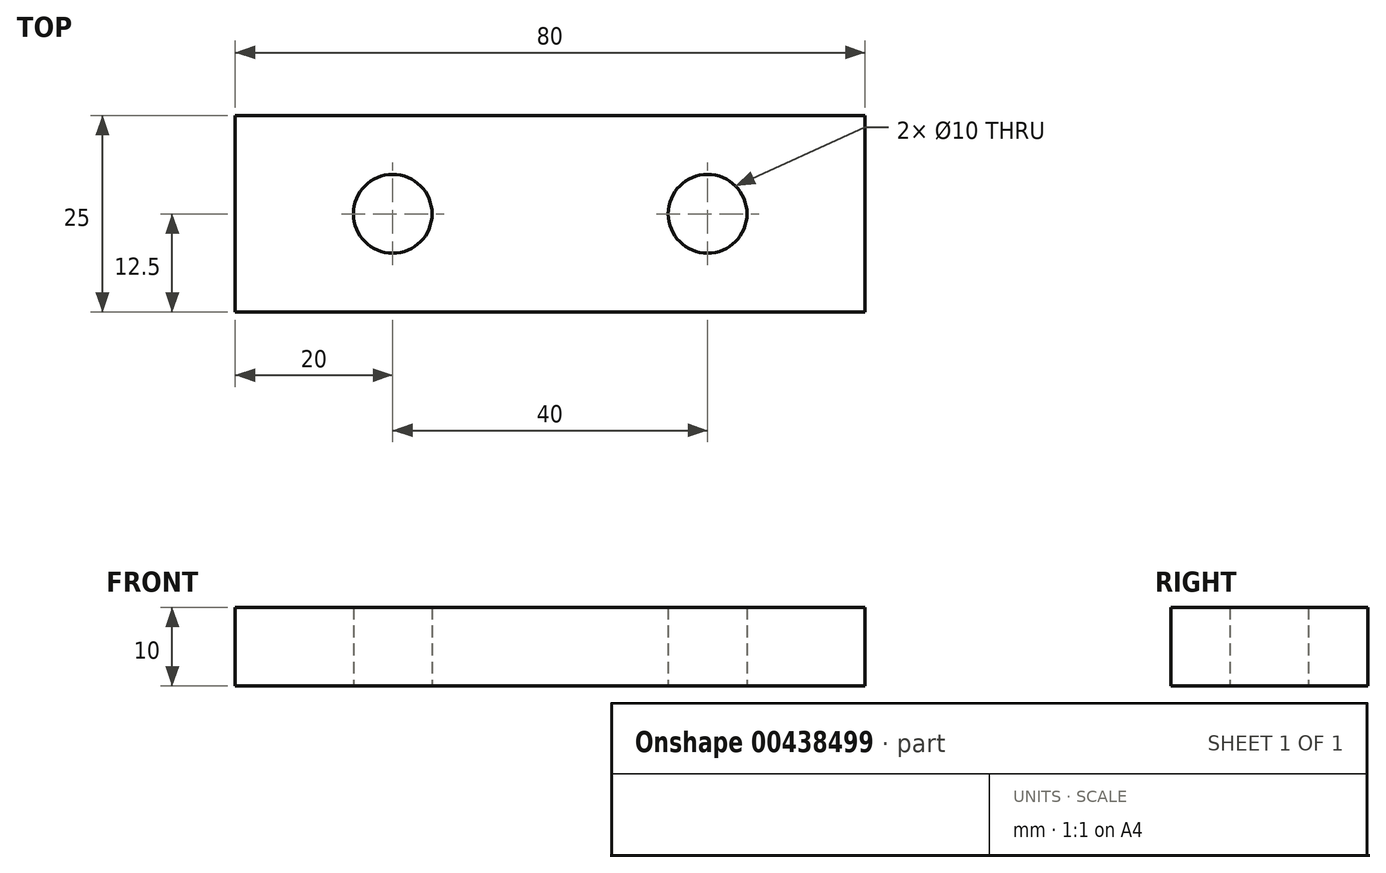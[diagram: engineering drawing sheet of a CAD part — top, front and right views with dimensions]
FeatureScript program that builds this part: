
annotation { "Feature Type Name" : "Feature", "Feature Type Description" : "" }
export const myFeature = defineFeature(function(context is Context, id is Id, definition is map)
    precondition{}
    {
        {
            var Q0;
            Q0=qCreatedBy(makeId("Top.planeOp"),FACE);
            var sketch = newSketch(context, id + "F0", { "sketchPlane" : qUnion([Q0])});
            skLineSegment(sketch, "E0.bottom", {"start": v(-66.6, 18.25) * mm, "end": v(-26.6, 18.25) * mm});
            skLineSegment(sketch, "E0.top", {"start": v(-66.6, -6.75) * mm, "end": v(-26.6, -6.75) * mm});
            skLineSegment(sketch, "E0.left", {"start": v(-66.6, 18.25) * mm, "end": v(-66.6, -6.75) * mm});
            skLineSegment(sketch, "E0.right", {"start": v(-26.6, 18.25) * mm, "end": v(-26.6, -6.75) * mm});
            skLineSegment(sketch, "E1.bottom", {"start": v(-26.6, 18.25) * mm, "end": v(13.4, 18.25) * mm});
            skLineSegment(sketch, "E1.top", {"start": v(-26.6, -6.75) * mm, "end": v(13.4, -6.75) * mm});
            skLineSegment(sketch, "E1.right", {"start": v(13.4, 18.25) * mm, "end": v(13.4, -6.75) * mm});
            skLineSegment(sketch, "E2.bottom", {"start": v(-46.6, -6.75) * mm, "end": v(-26.6, -6.75) * mm});
            skLineSegment(sketch, "E2.top", {"start": v(-46.6, -31.75) * mm, "end": v(-26.6, -31.75) * mm});
            skLineSegment(sketch, "E2.left", {"start": v(-46.6, -6.75) * mm, "end": v(-46.6, -31.75) * mm});
            skLineSegment(sketch, "E2.right", {"start": v(-26.6, -6.75) * mm, "end": v(-26.6, -31.75) * mm});
            skCircle(sketch, "E3", {"center": v(-46.6, 5.75) * mm, "radius": 5 * mm});
            skPoint(sketch, "E3.centerSnap0", {"position": v(-26.6, 5.75) * mm});
            skCircle(sketch, "E4", {"center": v(-6.6, 5.75) * mm, "radius": 5 * mm});
            skPoint(sketch, "E4.centerSnap0", {"position": v(-6.6, -6.75) * mm});
            skSolve(sketch);
        }
        {
            var Q0;
            Q0=makeQuery(id+"F0.imprint","IMPRINT",FACE,{"disambiguationData":[TD([[makeQuery(id+"F0.imprint","IMPRINT",EDGE,{"derivedFrom":sQuery(id+"F0.wireOp",EDGE,"E0.bottom")}),-1.0]])]});
            var Q1;
            Q1=makeQuery(id+"F0.imprint","IMPRINT",FACE,{"disambiguationData":[TD([[makeQuery(id+"F0.imprint","IMPRINT",EDGE,{"derivedFrom":sQuery(id+"F0.wireOp",EDGE,"E1.bottom")}),-1.0]])]});
            var Q2;
            Q2=makeQuery(id+"F0.imprint","IMPRINT",FACE,{"disambiguationData":[TD([[makeQuery(id+"F0.imprint","IMPRINT",EDGE,{"derivedFrom":sQuery(id+"F0.wireOp",EDGE,"E2.bottom")}),-1.0]])]});
            extrude(context, id + "F1", {"entities" : qUnion([Q0, Q1, Q2]), "depth" : 10 * mm});
        }
    });
